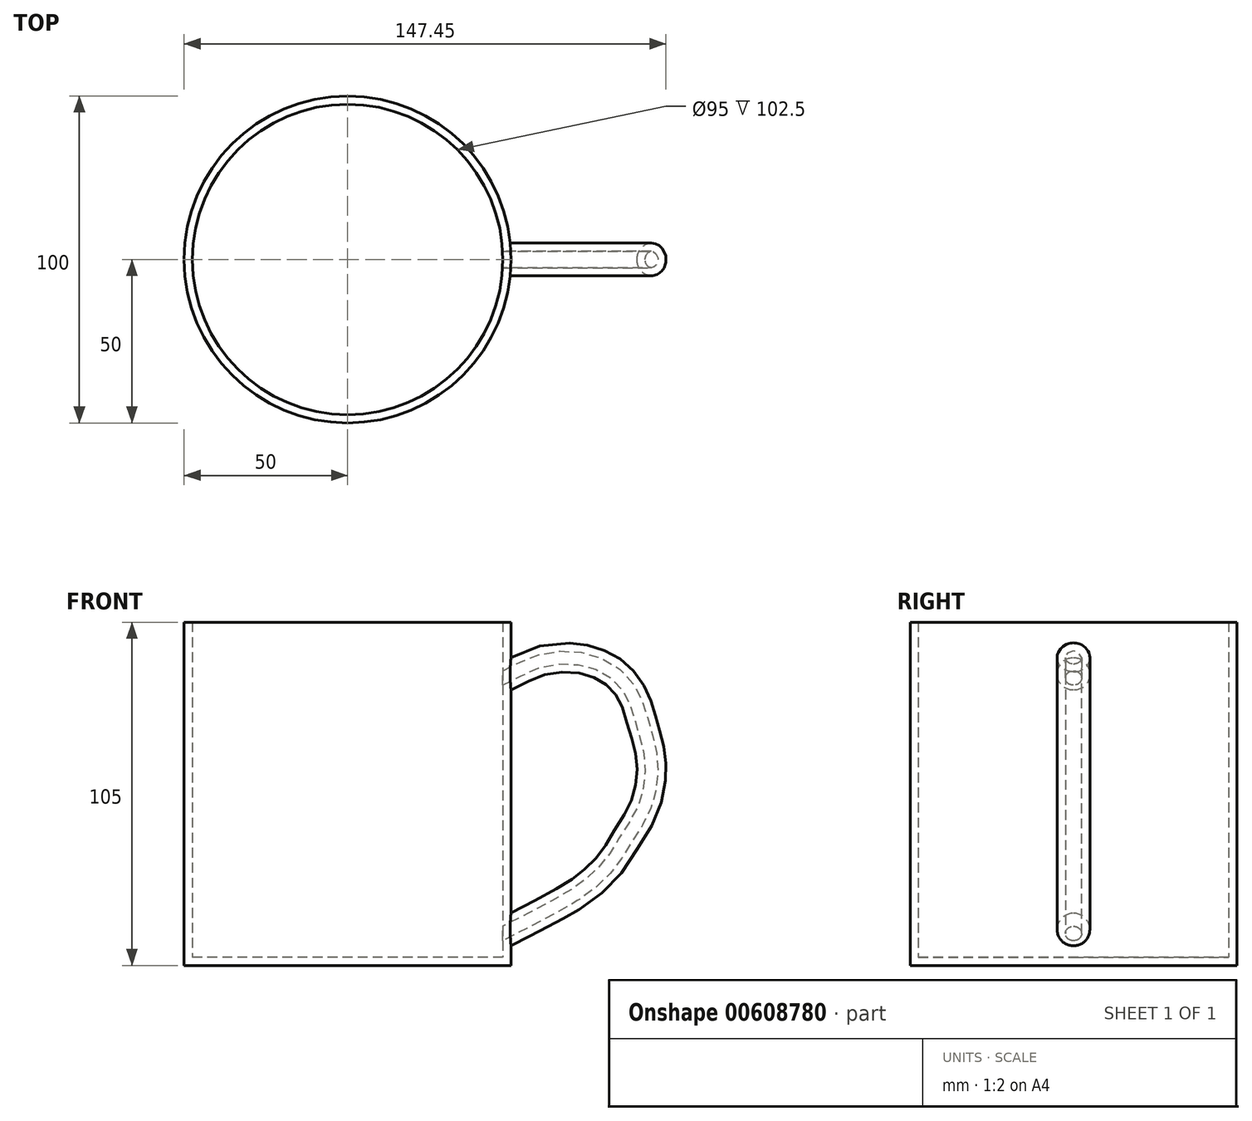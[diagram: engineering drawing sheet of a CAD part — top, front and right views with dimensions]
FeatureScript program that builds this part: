
annotation { "Feature Type Name" : "Feature", "Feature Type Description" : "" }
export const myFeature = defineFeature(function(context is Context, id is Id, definition is map)
    precondition{}
    {
        {
            var Q0;
            Q0=qCreatedBy(makeId("Top.planeOp"),FACE);
            var sketch = newSketch(context, id + "F0", { "sketchPlane" : qUnion([Q0])});
            skCircle(sketch, "E0", {"center": v(0, 0) * mm, "radius": 50 * mm});
            skSolve(sketch);
        }
        {
            var Q0;
            Q0 = qSketchRegion(id + "F0", true);
            extrude(context, id + "F1", {"entities" : qUnion([Q0]), "depth" : 105 * mm, "offsetDistance" : 25.4 * mm});
        }
        {
            var Q0;
            Q0=qCreatedBy(makeId("Right.planeOp"),FACE);
            cPlane(context, id + "F2", {"entities" : qUnion([Q0]), "cplaneType" : CPlaneType.OFFSET, "offset" : 50 * mm, "width" : 152.4 * mm, "height" : 152.4 * mm});
        }
        {
            var Q0;
            Q0=qCreatedBy(makeId("Front.planeOp"),FACE);
            var sketch = newSketch(context, id + "F3", { "sketchPlane" : qUnion([Q0])});
            skFitSpline(sketch, "E1", {"points": [v(49.43, 89.25) * mm, v(60.83, 93.86) * mm, v(73.32, 93.64) * mm, v(82.53, 89.04) * mm, v(87.79, 82.02) * mm, v(90.42, 74.35) * mm, v(92.6, 66.02) * mm, v(93.05, 56.6) * mm, v(90.42, 46.95) * mm, v(85.81, 39.06) * mm, v(80.33, 30.73) * mm, v(73.54, 24.15) * mm, v(65.87, 19.11) * mm, v(49.65, 10.56) * mm], "startDerivative": vector(131.36, 66.7) * mm, "endDerivative": vector(-173.88, -88.89) * mm});
            skSolve(sketch);
        }
        {
            var Q0;
            Q0=qCreatedBy(id+"F2.planeOp",FACE);
            var sketch = newSketch(context, id + "F4", { "sketchPlane" : qUnion([Q0])});
            skCircle(sketch, "E2", {"center": v(0, 89.23) * mm, "radius": 5 * mm});
            skCircle(sketch, "E3", {"center": v(0, 10.63) * mm, "radius": 5 * mm});
            skSolve(sketch);
        }
        {
            var Q0;
            Q0=makeQuery(id+"F4.imprint","IMPRINT",FACE,{"disambiguationData":[TD([[makeQuery(id+"F4.imprint","IMPRINT",EDGE,{"derivedFrom":sQuery(id+"F4.wireOp",EDGE,"E2")}),1.0]])]});
            var Q1;
            Q1=sQuery(id+"F3.wireOp",EDGE,"E1");
            sweep(context, id + "F5", {"operationType" : NewBodyOperationType.ADD, "profiles" : qUnion([Q0]), "path" : qUnion([Q1])});
        }
        {
            var Q0;
            Q0=makeQuery(id+"F1.opExtrude","CAP_FACE",FACE,{"disambiguationData":[OSD([sQuery(id+"F0.wireOp",EDGE,"E0")])],"isStart":false});
            shell(context, id + "F6", {"entities" : qUnion([Q0]), "thickness" : 2.5 * mm});
        }
    });
